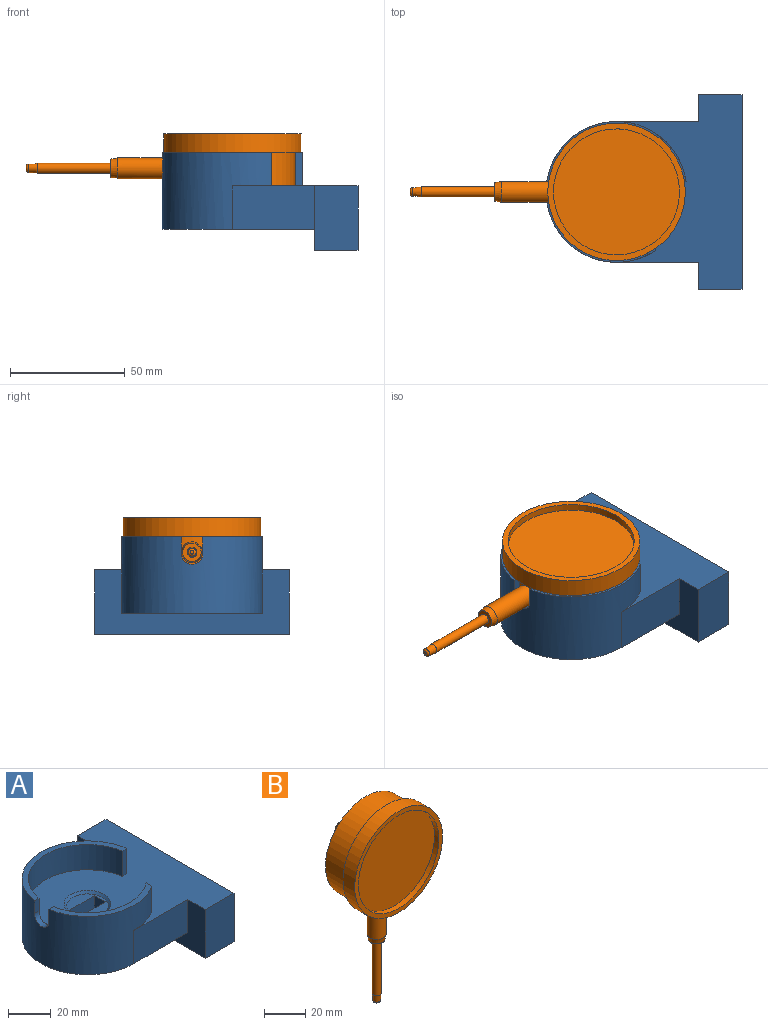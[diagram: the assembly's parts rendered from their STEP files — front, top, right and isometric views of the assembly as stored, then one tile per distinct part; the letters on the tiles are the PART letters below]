
ASSEMBLY  parts=2 mates=1
PART A: 24 faces, bbox 85.5x85x42.5 mm
  f0: cylinder r=30.75mm len=61.5mm, axis (0,0,-1), area 4024.7mm2, adj f2,f3,f13,f14,f15,f16,f19,f20
  f1: cylinder r=27.75mm len=55.5mm, axis (0,0,-1), area 1994.8mm2, adj f2,f3,f16,f19,f20,f21,f22,f23
  f2: plane 60.78x26.6mm, normal (0,0,1), area 248mm2, adj f0,f1,f20,f22
  f3: plane 47.37x25.95mm, normal (0,0,1), area 177.8mm2, adj f0,f1,f19,f23
  f4: plane 17.8x7.2mm, normal (-1,0,0), area 128.2mm2, adj f5,f7,f13,f17
  f5: plane 17.8x16.52mm, normal (0,1,0), area 294.1mm2, adj f4,f6,f13,f17
  f6: plane 17.8x7.2mm, normal (1,0,0), area 128.2mm2, adj f5,f7,f13,f17
  f7: plane 17.8x16.52mm, normal (0,-1,0), area 294.1mm2, adj f4,f6,f13,f17
  f8: plane 85x28mm, normal (-1,0,0), area 1211.5mm2, adj f9,f11,f12,f13,f14,f15,f16
  f9: plane 28x18.95mm, normal (0,-1,0), area 530.6mm2, adj f8,f10,f12,f16
  f10: plane 85x28mm, normal (1,0,0), area 2380mm2, adj f9,f11,f12,f16
  f11: plane 28x18.95mm, normal (0,1,0), area 530.6mm2, adj f8,f10,f12,f16
  f12: plane 85x18.95mm, normal (0,0,-1), area 1610.6mm2, adj f8,f9,f10,f11
  f13: plane 66.6x61.5mm, normal (0,0,-1), area 3571.1mm2, adj f0,f4,f5,f6,f7,f8,f14,f15
  f14: plane 35.85x19mm, normal (0,-1,0), area 681.1mm2, adj f0,f8,f13,f16
  f15: plane 35.85x19mm, normal (0,1,0), area 681.2mm2, adj f0,f8,f13,f16
  f16: plane 85x82.55mm, normal (0,0,1), area 4465.8mm2, adj f0,f1,f8,f9,f10,f11,f14,f15
  f17: plane 19.6x19.6mm, normal (0,0,1), area 182.8mm2, adj f4,f5,f6,f7,f18
  f18: cone r=9.5mm half-angle=45deg, axis (0,0,1), area 110.9mm2, adj f16,f17
  f19: plane 14.5x3.69mm, normal (1,0,0), area 53.5mm2, adj f0,f1,f3,f16
  f20: plane 14.5x2.97mm, normal (0.15,-0.99,0), area 43.5mm2, adj f0,f1,f2,f16
  f21: cylinder r=4.8mm len=9.6mm, axis (1,0,0), area 45.5mm2, adj f0,f1,f22,f23
  f22: plane 7.25x3.04mm, normal (0,-1,0), area 22mm2, adj f0,f1,f2,f21
  f23: plane 7.25x3.04mm, normal (0,1,0), area 22mm2, adj f0,f1,f3,f21
PART B: 26 faces, bbox 60x40x120.2 mm
  f0: plane 14.39x4.5mm, normal (0,1,0), area 46.4mm2, adj f22,f25
  f1: cylinder r=27.5mm len=55mm, axis (0,1,0), area 2440.6mm2, adj f2,f6,f8
  f2: plane 55x55mm, normal (0,1,0), area 2121.4mm2, adj f1,f15
  f3: cylinder r=30mm len=60mm, axis (0,1,0), area 1508mm2, adj f5,f6
  f4: cylinder r=27.5mm len=55mm, axis (0,1,0), area 518.4mm2, adj f5,f7
  f5: plane 60x60mm, normal (0,-1,0), area 451.6mm2, adj f3,f4
  f6: plane 60x60mm, normal (0,1,0), area 451.6mm2, adj f1,f3
  f7: plane 55x55mm, normal (0,-1,0), area 2375.8mm2, adj f4
  f8: cylinder r=4.53mm len=23.03mm, axis (0,0,1), area 650.6mm2, adj f1,f12
  f9: plane 1.62x1.62mm, normal (0,0,-1), area 2.1mm2, adj f14
  f10: cylinder r=2.16mm len=32mm, axis (0,0,1), area 434.8mm2, adj f11,f13
  f11: plane 8.01x8.01mm, normal (0,0,-1), area 35.7mm2, adj f10,f12
  f12: cone r=4.53mm half-angle=10deg, axis (0,0,1), area 81.7mm2, adj f8,f11
  f13: cone r=2.16mm half-angle=5deg, axis (0,0,1), area 51.1mm2, adj f10,f14
  f14: torus R=0.81mm, axis (0,0,1), area 13.3mm2, adj f9,f13
  f15: cylinder r=9mm len=18mm, axis (0,-1,0), area 56.5mm2, adj f2,f25
  f16: plane 14.39x4.5mm, normal (0,1,0), area 46.4mm2, adj f21,f25
  f17: cylinder r=8mm len=8mm, axis (1,0,0), area 88mm2, adj f18,f21,f22,f24
  f18: plane 7x0.5mm, normal (0,1,0), area 3.5mm2, adj f17,f19,f21,f22
  f19: cylinder r=8mm len=8mm, axis (1,0,0), area 88mm2, adj f18,f21,f22,f23
  f20: cylinder r=3.25mm len=7mm, axis (1,0,0), area 142.9mm2, adj f21,f22
  f21: plane 16.5x16.23mm, normal (1,0,0), area 195.5mm2, adj f16,f17,f18,f19,f20,f23,f24,f25
  f22: plane 16.5x16.23mm, normal (-1,0,0), area 195.5mm2, adj f0,f17,f18,f19,f20,f23,f24,f25
  f23: plane 8.23x7mm, normal (0,0,-1), area 53.7mm2, adj f19,f21,f22,f25
  f24: plane 8.23x7mm, normal (0,0,1), area 53.7mm2, adj f17,f21,f22,f25
  f25: torus R=8mm, axis (0,1,0), area 77.3mm2, adj f0,f15,f16,f21,f22,f23,f24
PLACE A t=(3.19,1.3,0)mm
PLACE B rot(axis=(-0.58,0.58,-0.58),120deg) t=(-6.81,1.3,26.72)mm
MATE slider B.f1 <-> A.f1  axis (0,0,-1) through (3.19,1.3,26.47)mm
